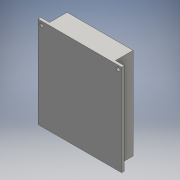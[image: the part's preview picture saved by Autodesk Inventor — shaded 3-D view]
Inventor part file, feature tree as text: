
AUTODESK INVENTOR PART (.ipt)
format: ipt  version: 2016 (Build 200138000, 138)  size: 107,008 bytes
history: native  units: mm
features: sketch x3, extrude x2, hole x1
ambient origin geometry x8: Origin, YZ Plane, XZ Plane, XY Plane, X Axis, Y Axis, Z Axis, Center Point
bodies: Solid1 (feature_tree)
feature tree (6):
  extrude  "Extrusion1"  Depth=104.0mm
  extrude  "Extrusion2"  Depth=75.0mm
  hole  "Hole1"  [1 undecoded]
  sketch  "Sketch1"  dims[d0=95.0mm d1=104.0mm]
  sketch  "Sketch2"  dims[d2=3.0mm d3=0.0mm d4=75.0mm]
  sketch  "Sketch3"  dims[d5=104.0mm d6=20.0mm d7=0.0mm d8=4.0mm d9=4.0mm d10=4.0mm d11=4.0mm d12=4.0mm d13=6.0mm d14=4.0mm d15=2.0mm d16=90.0deg d17=8.0mm d18=20.594885mm]
note: 1 required parameter value undecoded (feature->parameter linkage not recoverable at this tier; creation-order binding heuristic only, values carry confidence <= 0.55)
